# Revit family: Stex 35 Gewindeplatte GP
name_source: partatom
category: HLS-Bauteile
revit_build: Autodesk Revit 2017 (Build: 20190507_1515(x64)
units: mm (PartAtom-declared; Revit-internal decimal feet)

## family parameters
Arbeitsebenenbasiert = Ja
Beim Laden mit Abzugskörper schneiden = Nein
Bemaßung runder Anschluss = Durchmesser verwenden
Gemeinsam genutzt = Ja
Immer vertikal = Nein
Raumberechnungspunkt = Nein
Teiletyp = Normal

## types (2) — shared parameters
Anzugsmoment = 0.00 kN-m
Fabrikat = MEFA
Firma = MEFA Befestigungs- und Montagesysteme GmbH
Gewicht = 0.04 kg
Gewicht pro Bauteil = 0.04 kg
Kurztext1 = Stex Gewindeplatte GP 35
Material = Stahl
Mengeneinheit = St
Oberflaeche = galvanisch verzinkt
Profiltyp = Stex 35
Vorgabe-Ansicht = 1219 mm
vpe = 50 St
zero-valued in all types: Länge Gewinde

## per-type parameters (varying)
| type | Artikelnummer | EAN | Gewinde | Gewindeplatte | Kurztext2 |
| Stex-Gewindeplatte M10 | 127201101 | 4250928424327 | M10 | MEFA Gewindeplatte 35 für Stex 35 : MEFA Gewindeplatte 35 für Stex 35 M10 | M10 gvz |
| Stex-Gewindeplatte M 8 | 127201001 | 4250928424310 | M8 | MEFA Gewindeplatte 35 für Stex 35 : MEFA Gewindeplatte 35 für Stex 35 M 8 | M8 gvz |
